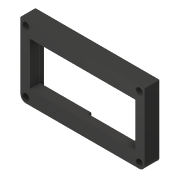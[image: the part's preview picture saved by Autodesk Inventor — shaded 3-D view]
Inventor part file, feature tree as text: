
AUTODESK INVENTOR PART (.ipt)
format: ipt  version: 2020 (Build 240168000, 168)  size: 182,784 bytes
history: native  units: in
note: dims shown in document units (in); Inventor stores cm internally (conversion verified against a paired STEP export)
features: sketch x6, extrude x4, plane x4, projected_geometry x4, hole x2, fillet x1
ambient origin geometry x8: Origin, YZ Plane, XZ Plane, XY Plane, X Axis, Y Axis, Z Axis, Center Point
bodies: Solid1 (feature_tree)
feature tree (21):
  extrude  "Extrusion1"  Depth=0.1in TaperAngle=0.0deg
  plane  "Work Plane14"
  extrude  "Extrusion2"  Depth=0.1in TaperAngle=0.0deg
  plane  "Work Plane15"
  extrude  "Extrusion6"  Depth=1.682in
  hole  "Hole1"  [1 undecoded]
  sketch  "Sketch5"  dims[d23=0.1875in d24=-0.0625in d35=1.682in]
  extrude  "Extrusion4"  Depth=0.305in
  fillet  "Fillet1"  Radius=0.299in
  plane  "Work Plane13"
  plane  "Work Plane5"
  hole  "Hole3"  [1 undecoded]
  sketch  "Sketch1"  dims[d2=0.372in d3=0.0in d6=0.1in d7=0.0in]
  sketch  "Sketch2"  dims[d11=0.1875in]
  sketch  "Sketch4"  dims[d12=0.12in d13=0.75in d14=0.25in d15=0.001in d16=0.5635in d17=1.0in d18=0.8108in d21=0.1in d22=0.0in]
  projected_geometry  "Projected Loop1"
  projected_geometry  "Projected Loop2"
  projected_geometry  "Projected Loop3"
  projected_geometry  "Projected Loop4"
  sketch  "Sketch8"  dims[d36=0.392in d38=1.587in]
  sketch  "Sketch9"  dims[d39=3.842in d40=0.305in d53=0.299in d54=2.411in d55=0.105in d56=3.902in d57=0.166in d58=0.0in d60=0.225in d61=0.42in d62=3.66in d63=2.165in d64=0.089in d65=0.75in d66=0.256in d67=0.118in d68=90.0deg d69=0.25in d70=0.0in d41=0.5in d42=0.0344in d43=0.5in d44=0.0344in]
note: 2 required parameter values undecoded (feature->parameter linkage not recoverable at this tier; creation-order binding heuristic only, values carry confidence <= 0.55)
